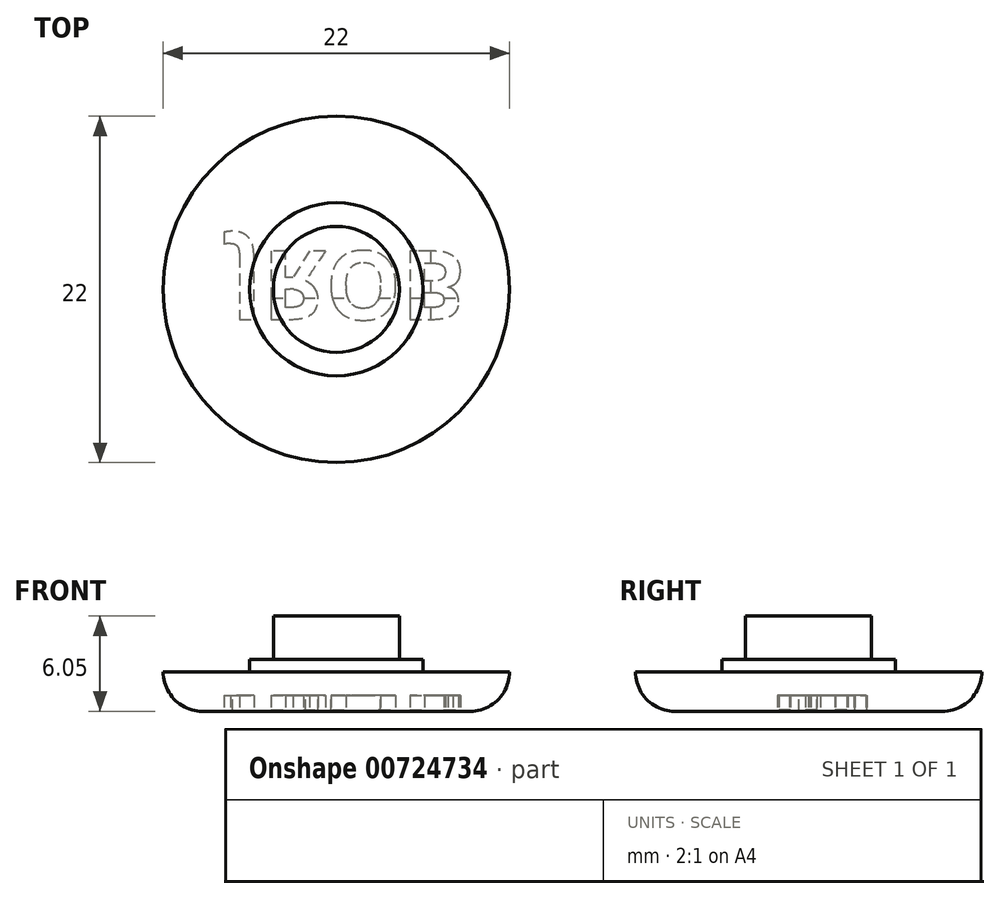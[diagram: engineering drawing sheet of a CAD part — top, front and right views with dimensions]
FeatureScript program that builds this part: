
annotation { "Feature Type Name" : "Feature", "Feature Type Description" : "" }
export const myFeature = defineFeature(function(context is Context, id is Id, definition is map)
    precondition{}
    {
        {
            var Q0;
            Q0=qCreatedBy(makeId("Top.planeOp"),FACE);
            var sketch = newSketch(context, id + "F0", { "sketchPlane" : qUnion([Q0])});
            skCircle(sketch, "E0", {"center": v(0, 0) * mm, "radius": 11 * mm});
            skCircle(sketch, "E1", {"center": v(0, 0) * mm, "radius": 4 * mm});
            skCircle(sketch, "E2", {"center": v(0, 0) * mm, "radius": 5.5 * mm});
            skSolve(sketch);
        }
        {
            var Q0;
            Q0=makeQuery(id+"F0.imprint","IMPRINT",FACE,{"disambiguationData":[TD([[makeQuery(id+"F0.imprint","IMPRINT",EDGE,{"derivedFrom":sQuery(id+"F0.wireOp",EDGE,"E0")}),1.0]])]});
            extrude(context, id + "F1", {"entities" : qUnion([Q0]), "depth" : 2.5 * mm, "offsetDistance" : 25 * mm});
        }
        {
            var Q0;
            Q0=makeQuery(id+"F0.imprint","IMPRINT",FACE,{"disambiguationData":[TD([[makeQuery(id+"F0.imprint","IMPRINT",EDGE,{"derivedFrom":sQuery(id+"F0.wireOp",EDGE,"E1")}),-1.0]])]});
            var Q1;
            Q1=makeQuery(id+"F1.opExtrude","CAP_FACE",FACE,{"disambiguationData":[OSD([sQuery(id+"F0.wireOp",EDGE,"E0"),sQuery(id+"F0.wireOp",EDGE,"E2")])],"isStart":false});
            extrude(context, id + "F2", {"entities" : qUnion([Q0]), "operationType" : NewBodyOperationType.ADD, "endBound" : BoundingType.UP_TO_SURFACE, "depth" : 25 * mm, "endBoundEntityFace" : qUnion([Q1]), "hasOffset" : true, "offsetDistance" : .8 * mm, "offsetOppositeDirection" : true});
        }
        {
            var Q0;
            Q0=makeQuery(id+"F0.imprint","IMPRINT",FACE,{"disambiguationData":[TD([[makeQuery(id+"F0.imprint","IMPRINT",EDGE,{"derivedFrom":sQuery(id+"F0.wireOp",EDGE,"E1")}),1.0]])]});
            var Q1;
            Q1=makeQuery(id+"F2.opExtrude","CAP_FACE",FACE,{"disambiguationData":[OSD([sQuery(id+"F0.wireOp",EDGE,"E0"),sQuery(id+"F0.wireOp",EDGE,"E2")])],"isStart":false});
            extrude(context, id + "F3", {"entities" : qUnion([Q0]), "operationType" : NewBodyOperationType.ADD, "endBound" : BoundingType.UP_TO_SURFACE, "depth" : 3 * mm, "endBoundEntityFace" : qUnion([Q1]), "hasOffset" : true, "offsetDistance" : 2.75 * mm, "offsetOppositeDirection" : true});
        }
        {
            var Q0;
            {var subQ0=sQuery(id+"F0.wireOp",EDGE,"E1");var subQ1=sQuery(id+"F0.wireOp",EDGE,"E2");Q0=makeQuery(id+"F3.boolean.opBoolean","MERGE",FACE,{"derivedFrom":[makeQuery(id+"F2.boolean.opBoolean","MERGE",FACE,{"derivedFrom":[makeQuery(id+"F1.opExtrude","CAP_FACE",FACE,{"disambiguationData":[OSD([sQuery(id+"F0.wireOp",EDGE,"E0"),subQ1])],"isStart":true}),makeQuery(id+"F2.opExtrude","CAP_FACE",FACE,{"disambiguationData":[OSD([subQ0,subQ1])],"isStart":true})]}),makeQuery(id+"F3.opExtrude","CAP_FACE",FACE,{"disambiguationData":[OSD([subQ0])],"isStart":true})]});}
            fillet(context, id + "F4", {"entities" : qUnion([Q0]), "radius" : 2.5 * mm, "tangentPropagation" : true, "allowEdgeOverflow" : false});
        }
        {
            var Q0;
            Q0=qCreatedBy(makeId("Right.planeOp"),FACE);
            var sketch = newSketch(context, id + "F5", { "sketchPlane" : qUnion([Q0])});
            skEllipse(sketch, "E3", {"center": v(-63.43, -1.89) * mm, "majorRadius": 11 * mm, "minorRadius": 2.5 * mm, "majorAxis": v(-1, 0)});
            skPoint(sketch, "E4", {"position": v(-63.43, 0.61) * mm});
            skLineSegment(sketch, "E5", {"start": v(-55.79, 0) * mm, "end": v(-71.08, 0) * mm});
            skArc(sketch, "E6", {"start": v(-11, 2.37) * mm, "mid": v(-6, 2.57) * mm, "end": v(-11, 2.5) * mm});
            skArc(sketch, "E7", {"start": v(6, 2.5) * mm, "mid": v(6, 2.46) * mm, "end": v(6, 2.42) * mm});
            skLineSegment(sketch, "E8", {"start": v(-63.43, 0.61) * mm, "end": v(-63.43, -4.39) * mm});
            skPoint(sketch, "E9.orphan", {"position": v(-63.43, -3.78) * mm});
            skPoint(sketch, "E10.orphan", {"position": v(-63.43, 0) * mm});
            skSolve(sketch);
        }
        {
            var Q0;
            {var subQ0=sQuery(id+"F0.wireOp",EDGE,"E1");var subQ1=sQuery(id+"F0.wireOp",EDGE,"E2");Q0=makeQuery(id+"F3.boolean.opBoolean","MERGE",FACE,{"derivedFrom":[makeQuery(id+"F2.boolean.opBoolean","MERGE",FACE,{"derivedFrom":[makeQuery(id+"F1.opExtrude","CAP_FACE",FACE,{"disambiguationData":[OSD([sQuery(id+"F0.wireOp",EDGE,"E0"),subQ1])],"isStart":true}),makeQuery(id+"F2.opExtrude","CAP_FACE",FACE,{"disambiguationData":[OSD([subQ0,subQ1])],"isStart":true})]}),makeQuery(id+"F3.opExtrude","CAP_FACE",FACE,{"disambiguationData":[OSD([subQ0])],"isStart":true})]});}
            var sketch = newSketch(context, id + "F6", { "sketchPlane" : qUnion([Q0])});
            skSolve(sketch);
        }
        {
            var Q0;
            {var subQ0=sQuery(id+"F0.wireOp",EDGE,"E1");var subQ1=sQuery(id+"F0.wireOp",EDGE,"E2");var subQ2=sQuery(id+"F0.wireOp",EDGE,"E0");Q0=makeQuery(id+"F6.imprint","IMPRINT",FACE,{"disambiguationData":[TD([[makeQuery(id+"F6.imprint","IMPRINT",EDGE,{"derivedFrom":makeQuery(id+"F4.opFillet","BLEND_EDGE",EDGE,{"blendedFrom":[makeQuery(id+"F1.opExtrude","CAP_EDGE",EDGE,{"disambiguationData":[OSD([subQ2])],"isStart":true}),makeQuery(id+"F3.boolean.opBoolean","MERGE",FACE,{"derivedFrom":[makeQuery(id+"F2.boolean.opBoolean","MERGE",FACE,{"derivedFrom":[makeQuery(id+"F1.opExtrude","CAP_FACE",FACE,{"disambiguationData":[OSD([subQ2,subQ1])],"isStart":true}),makeQuery(id+"F2.opExtrude","CAP_FACE",FACE,{"disambiguationData":[OSD([subQ0,subQ1])],"isStart":true})]}),makeQuery(id+"F3.opExtrude","CAP_FACE",FACE,{"disambiguationData":[OSD([subQ0])],"isStart":true})]})],"blendedInto":[makeQuery(id+"F3.boolean.opBoolean","MERGE",FACE,{"derivedFrom":[makeQuery(id+"F2.boolean.opBoolean","MERGE",FACE,{"derivedFrom":[makeQuery(id+"F1.opExtrude","CAP_FACE",FACE,{"disambiguationData":[OSD([subQ2,subQ1])],"isStart":true}),makeQuery(id+"F2.opExtrude","CAP_FACE",FACE,{"disambiguationData":[OSD([subQ0,subQ1])],"isStart":true})]}),makeQuery(id+"F3.opExtrude","CAP_FACE",FACE,{"disambiguationData":[OSD([subQ0])],"isStart":true})]})]})}),1.0]])]});}
            var sketch = newSketch(context, id + "F7", { "sketchPlane" : qUnion([Q0])});
            skLineSegment(sketch, "E11", {"start": v(-8.5, 0) * mm, "end": v(8.5, 0) * mm});
            skText(sketch, "E12", { "text": " JROB", "fontName": "OpenSans-Bold.ttf"});
            const initialGuessF7  = {"E12": [-0.00827, -0.00242, 1, 0, 0.00436]};
            skSetInitialGuess(sketch, initialGuessF7);
            skSolve(sketch);
        }
        {
            var Q0;
            Q0=qSketchRegion(id+"F7",true);
            extrude(context, id + "F8", {"entities" : qUnion([Q0]), "operationType" : NewBodyOperationType.REMOVE, "oppositeDirection" : true, "depth" : 1 * mm, "offsetDistance" : 25 * mm});
        }
        {
            var Q0;
            {var subQ0=sQuery(id+"F0.wireOp",EDGE,"E1");var subQ1=sQuery(id+"F0.wireOp",EDGE,"E2");var subQ2=sQuery(id+"F0.wireOp",EDGE,"E0");Q0=makeQuery(id+"F6.imprint","IMPRINT",FACE,{"disambiguationData":[TD([[makeQuery(id+"F6.imprint","IMPRINT",EDGE,{"derivedFrom":makeQuery(id+"F4.opFillet","BLEND_EDGE",EDGE,{"blendedFrom":[makeQuery(id+"F1.opExtrude","CAP_EDGE",EDGE,{"disambiguationData":[OSD([subQ2])],"isStart":true}),makeQuery(id+"F3.boolean.opBoolean","MERGE",FACE,{"derivedFrom":[makeQuery(id+"F2.boolean.opBoolean","MERGE",FACE,{"derivedFrom":[makeQuery(id+"F1.opExtrude","CAP_FACE",FACE,{"disambiguationData":[OSD([subQ2,subQ1])],"isStart":true}),makeQuery(id+"F2.opExtrude","CAP_FACE",FACE,{"disambiguationData":[OSD([subQ0,subQ1])],"isStart":true})]}),makeQuery(id+"F3.opExtrude","CAP_FACE",FACE,{"disambiguationData":[OSD([subQ0])],"isStart":true})]})],"blendedInto":[makeQuery(id+"F3.boolean.opBoolean","MERGE",FACE,{"derivedFrom":[makeQuery(id+"F2.boolean.opBoolean","MERGE",FACE,{"derivedFrom":[makeQuery(id+"F1.opExtrude","CAP_FACE",FACE,{"disambiguationData":[OSD([subQ2,subQ1])],"isStart":true}),makeQuery(id+"F2.opExtrude","CAP_FACE",FACE,{"disambiguationData":[OSD([subQ0,subQ1])],"isStart":true})]}),makeQuery(id+"F3.opExtrude","CAP_FACE",FACE,{"disambiguationData":[OSD([subQ0])],"isStart":true})]})]})}),1.0]])]});}
            var sketch = newSketch(context, id + "F9", { "sketchPlane" : qUnion([Q0])});
            skLineSegment(sketch, "E13.bottom", {"start": v(-4.93, 0.55) * mm, "end": v(8.07, 0.55) * mm});
            skLineSegment(sketch, "E13.top", {"start": v(-4.93, 0.54) * mm, "end": v(8.07, 0.54) * mm});
            skLineSegment(sketch, "E13.left", {"start": v(-4.93, 0.55) * mm, "end": v(-4.93, 0.54) * mm});
            skLineSegment(sketch, "E13.right", {"start": v(8.07, 0.55) * mm, "end": v(8.07, 0.54) * mm});
            skLineSegment(sketch, "E14.bottom", {"start": v(5.98, -2.87) * mm, "end": v(5.97, -2.87) * mm});
            skLineSegment(sketch, "E14.top", {"start": v(5.98, 2.35) * mm, "end": v(5.97, 2.35) * mm});
            skLineSegment(sketch, "E14.left", {"start": v(5.98, -2.87) * mm, "end": v(5.98, 2.35) * mm});
            skLineSegment(sketch, "E14.right", {"start": v(5.97, -2.87) * mm, "end": v(5.97, 2.35) * mm});
            skPoint(sketch, "E14.middle", {"position": v(5.98, -0.26) * mm});
            skSolve(sketch);
        }
        {
            var Q0;
            Q0 = qSketchRegion(id + "F9", true);
            extrude(context, id + "F10", {"entities" : qUnion([Q0]), "operationType" : NewBodyOperationType.ADD, "oppositeDirection" : true, "depth" : .1 * mm, "offsetDistance" : 25 * mm});
        }
    });
